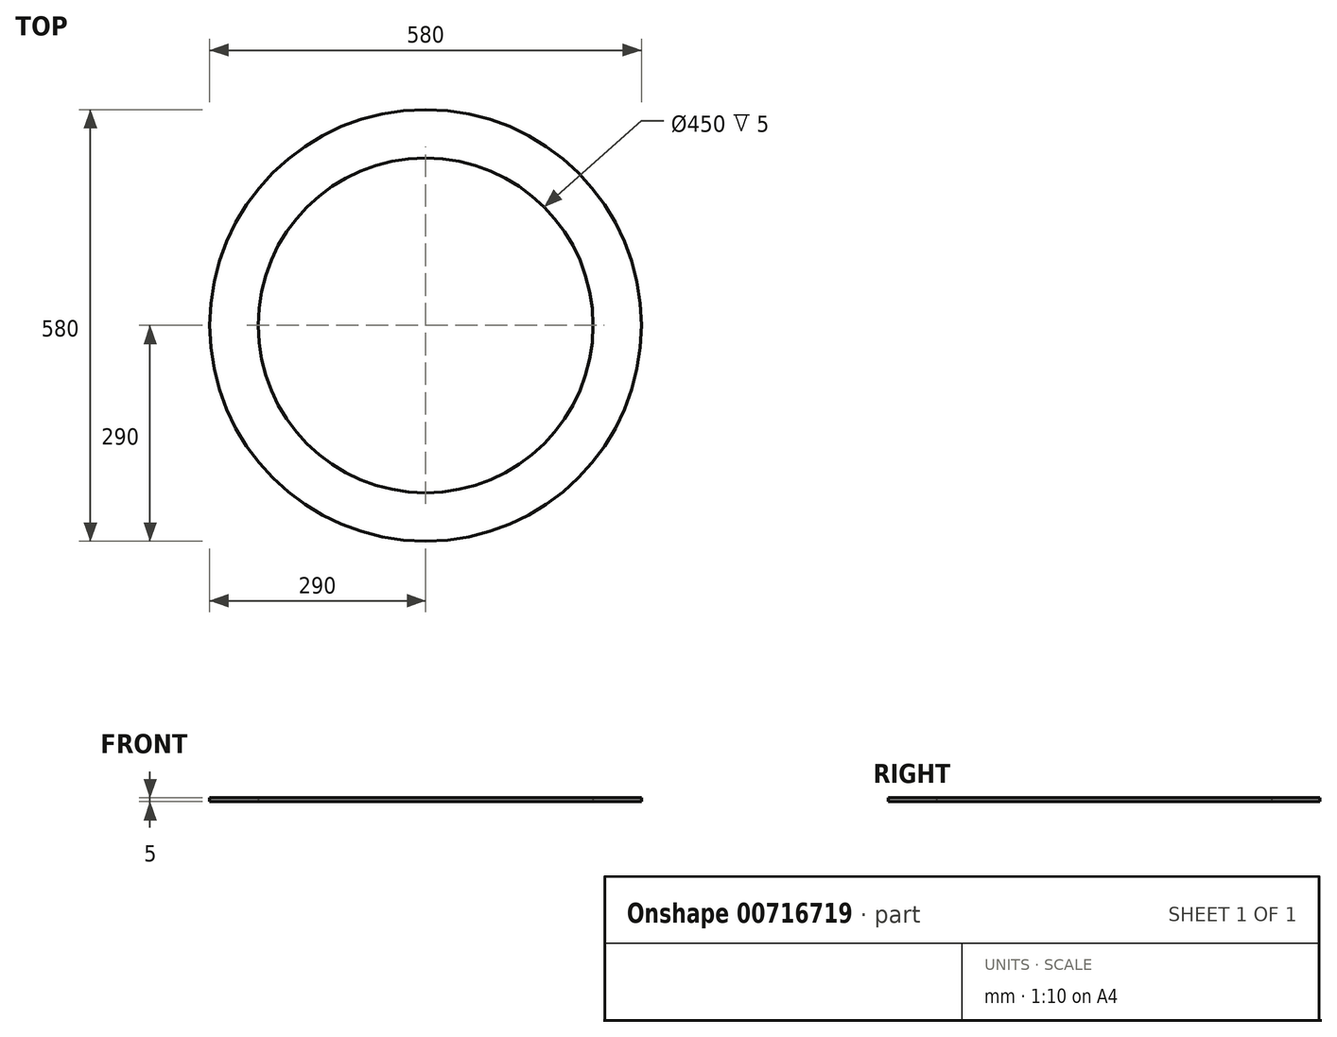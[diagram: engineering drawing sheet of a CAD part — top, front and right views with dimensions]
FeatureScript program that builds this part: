
annotation { "Feature Type Name" : "Feature", "Feature Type Description" : "" }
export const myFeature = defineFeature(function(context is Context, id is Id, definition is map)
    precondition{}
    {
        {
            var Q0;
            Q0=qCreatedBy(makeId("Top.planeOp"),FACE);
            var sketch = newSketch(context, id + "F0", { "sketchPlane" : qUnion([Q0])});
            skCircle(sketch, "E0", {"center": v(0, 0) * mm, "radius": 290 * mm});
            skCircle(sketch, "E1", {"center": v(0, 0) * mm, "radius": 225 * mm});
            skSolve(sketch);
        }
        {
            var Q0;
            Q0=makeQuery(id+"F0.imprint","IMPRINT",FACE,{"disambiguationData":[TD([[makeQuery(id+"F0.imprint","IMPRINT",EDGE,{"derivedFrom":sQuery(id+"F0.wireOp",EDGE,"E0")}),1.0]])]});
            extrude(context, id + "F1", {"entities" : qUnion([Q0]), "depth" : 5 * mm, "offsetDistance" : 25 * mm});
        }
    });
